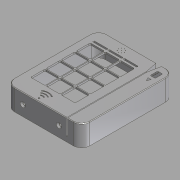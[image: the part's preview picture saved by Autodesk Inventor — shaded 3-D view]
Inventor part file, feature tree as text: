
AUTODESK INVENTOR PART (.ipt)
format: ipt  version: 2014 SP2 (Build 180246200, 246)  size: 481,792 bytes
history: native  units: mm
features: projected_geometry x9, sketch x8, extrude x7, fillet x3, hole x2, pattern_linear x2, other x1, shell x1, chamfer x1
ambient origin geometry x8: Origin, YZ Plane, XZ Plane, XY Plane, X Axis, Y Axis, Z Axis, Center Point
bodies: Body1 (feature_tree)
feature tree (34):
  other  "Těleso1"
  extrude  "Vysunutí1"  Depth=90.0mm
  fillet  "Zaoblení1"  Radius=110.0mm
  extrude  "Vysunutí2"  Depth=25.0mm TaperAngle=0.0deg
  extrude  "Vysunutí3"  Depth=10.0mm
  sketch  "Náčrt7"
  shell  "Skořepina1"  Thickness=1.0mm
  extrude  "Vysunutí4"  Depth=72.0mm
  hole  "Díra1"  [1 undecoded]
  chamfer  "Zkosení1"  Distance=3.0mm
  extrude  "Vysunutí5"  Depth=15.0mm
  pattern_linear  "Obdélníkové pole1"  Spacing1=3.0mm  [1 undecoded]
  hole  "Díra2"  [1 undecoded]
  extrude  "Vysunutí6"  Depth=19.0mm TaperAngle=0.0deg
  fillet  "Zaoblení3"  Radius=17.0mm
  extrude  "Vysunutí7"  Depth=17.0mm
  fillet  "Zaoblení4"  Radius=18.7mm
  pattern_linear  "Obdélníkové pole2"  Spacing1=9.0mm  [1 undecoded]
  sketch  "Náčrt4"
  sketch  "Náčrt5"
  projected_geometry  "Promítnutá smyčka1"
  sketch  "Náčrt6"
  projected_geometry  "Promítnutá smyčka2"
  projected_geometry  "Promítnutá smyčka3"
  projected_geometry  "Promítnutá smyčka4"
  projected_geometry  "Promítnutá smyčka5"
  sketch  "Náčrt8"
  projected_geometry  "Promítnutá smyčka6"
  projected_geometry  "Promítnutá smyčka7"
  sketch  "Náčrt10"
  projected_geometry  "Promítnutá smyčka8"
  sketch  "Náčrt11"
  sketch  "Náčrt12"
  projected_geometry  "Promítnutá smyčka9"
note: 4 required parameter values undecoded (feature->parameter linkage not recoverable at this tier; creation-order binding heuristic only, values carry confidence <= 0.55)
